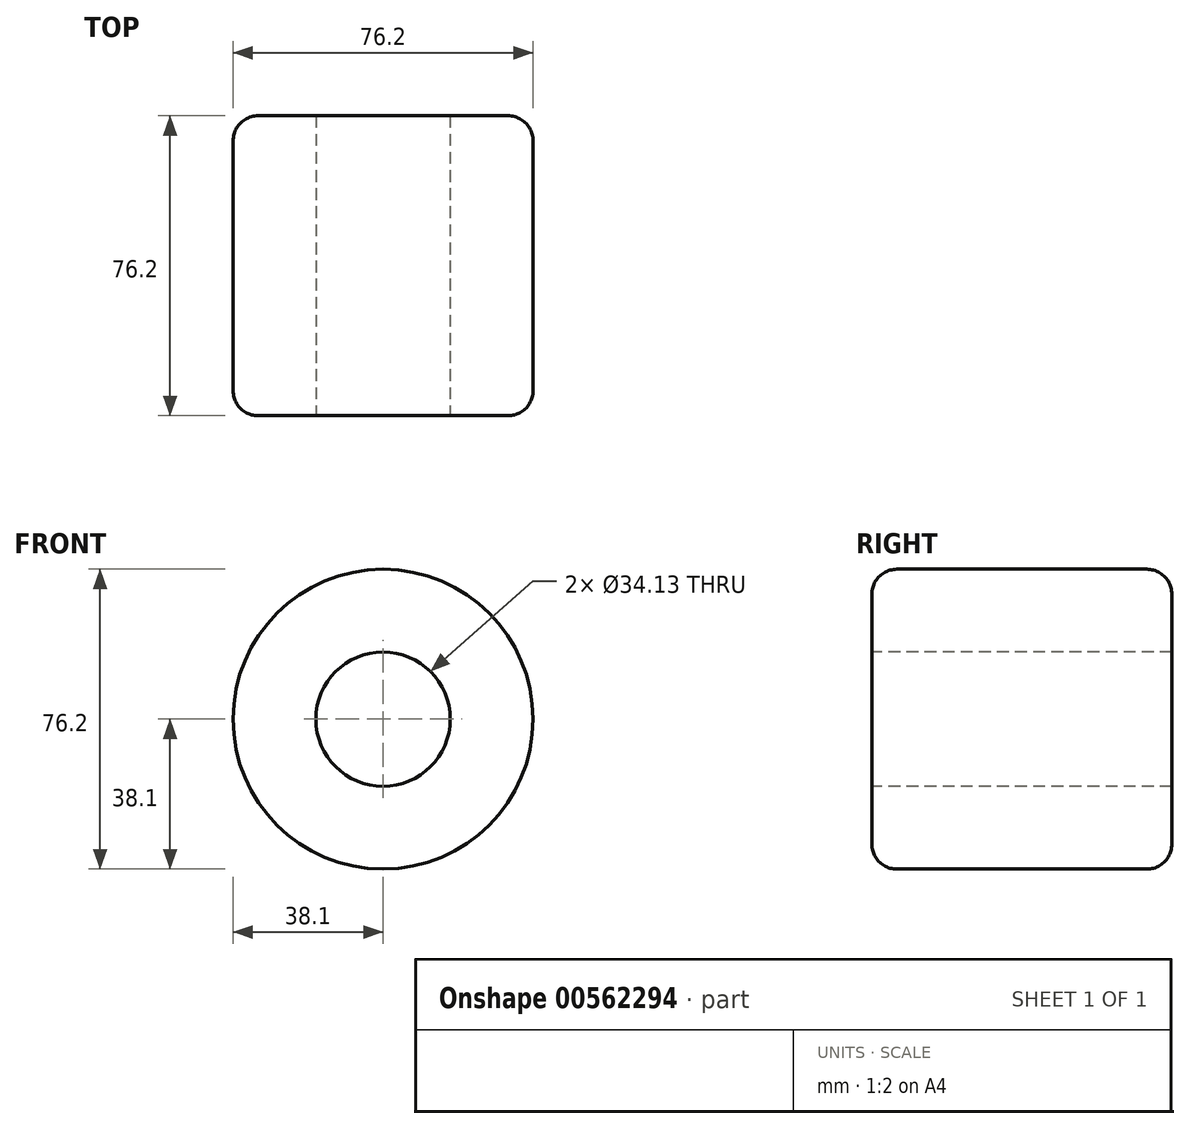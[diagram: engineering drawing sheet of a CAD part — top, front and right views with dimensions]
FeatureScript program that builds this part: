
annotation { "Feature Type Name" : "Feature", "Feature Type Description" : "" }
export const myFeature = defineFeature(function(context is Context, id is Id, definition is map)
    precondition{}
    {
        {
            var Q0;
            Q0=qCreatedBy(makeId("Front.planeOp"),FACE);
            var sketch = newSketch(context, id + "F0", { "sketchPlane" : qUnion([Q0])});
            skCircle(sketch, "E0", {"center": v(0, 0) * mm, "radius": 38.1 * mm});
            skSolve(sketch);
        }
        {
            var Q0;
            Q0=makeQuery(id+"F0.imprint","IMPRINT",FACE,{"disambiguationData":[TD([[makeQuery(id+"F0.imprint","IMPRINT",EDGE,{"derivedFrom":sQuery(id+"F0.wireOp",EDGE,"E0")}),1.0]])]});
            extrude(context, id + "F1", {"entities" : qUnion([Q0]), "endBound" : BoundingType.SYMMETRIC, "depth" : 76.2 * mm, "offsetDistance" : 25.4 * mm});
        }
        {
            var Q0;
            Q0=makeQuery(id+"F1.opExtrude","CAP_FACE",FACE,{"disambiguationData":[OSD([sQuery(id+"F0.wireOp",EDGE,"E0")])],"isStart":false});
            var sketch = newSketch(context, id + "F2", { "sketchPlane" : qUnion([Q0])});
            skPoint(sketch, "E1", {"position": v(0, 0) * mm});
            skSolve(sketch);
        }
        {
            var Q0;
            Q0=sQuery(id+"F2.wireOp",VERTEX,"E1");
            var Q1;
            Q1=makeQuery(id+"F1.opExtrude","SWEPT_BODY",BODY,{"disambiguationData":[OSD([sQuery(id+"F0.wireOp",EDGE,"E0")])]});
            hole(context, id + "F3", {"style" : HoleStyle.SIMPLE, "endStyle" : HoleEndStyle.THROUGH, "standardTappedOrClearance" : lookupTablePath({ "standard" : "ANSI", "engagement" : "75%", "pitch" : "6 tpi", "size" : "1 1/2", "type" : "Tapped" }), "standardBlindInLast" : lookupTablePath({ "standard" : "ANSI", "engagement" : "75%", "pitch" : "6 tpi", "size" : "1 1/2", "type" : "Tapped" }), "holeDiameter" : 34.13 * mm, "showTappedDepth" : true, "isTappedThrough" : true, "tappedDepth" : 34.3 * mm, "tapClearance" : 3, "locations" : qUnion([Q0]), "scope" : qUnion([Q1]), "majorDiameter" : 38.1 * mm});
        }
        {
            var Q0;
            Q0=makeQuery(id+"F1.opExtrude","CAP_EDGE",EDGE,{"disambiguationData":[OSD([sQuery(id+"F0.wireOp",EDGE,"E0")])],"isStart":false});
            var Q1;
            Q1=makeQuery(id+"F1.opExtrude","CAP_EDGE",EDGE,{"disambiguationData":[OSD([sQuery(id+"F0.wireOp",EDGE,"E0")])],"isStart":true});
            var Q2;
            Q2=makeQuery(id+"F3.hole-0.boolean.opBoolean","COPY",EDGE,{"derivedFrom":makeQuery(id+"F3.hole-0.opRevolve","SWEPT_EDGE",EDGE,{"disambiguationData":[OSD([sQuery(id+"F3.hole-0.sketch.wireOp",EDGE,"core_line_2"),sQuery(id+"F3.hole-0.sketch.wireOp",EDGE,"core_line_3")])]})});
            var Q3;
            Q3=makeQuery(id+"F3.hole-0.boolean.opBoolean","INTERSECT",EDGE,{"derivedFrom":[makeQuery(id+"F1.opExtrude","CAP_FACE",FACE,{"disambiguationData":[OSD([sQuery(id+"F0.wireOp",EDGE,"E0")])],"isStart":true}),makeQuery(id+"F3.hole-0.opRevolve","SWEPT_FACE",FACE,{"disambiguationData":[OSD([sQuery(id+"F3.hole-0.sketch.wireOp",EDGE,"core_line_2")])]})]});
            fillet(context, id + "F4", {"entities" : qUnion([Q0, Q1, Q2, Q3]), "radius" : 6.35 * mm, "tangentPropagation" : true, "allowEdgeOverflow" : false});
        }
    });
